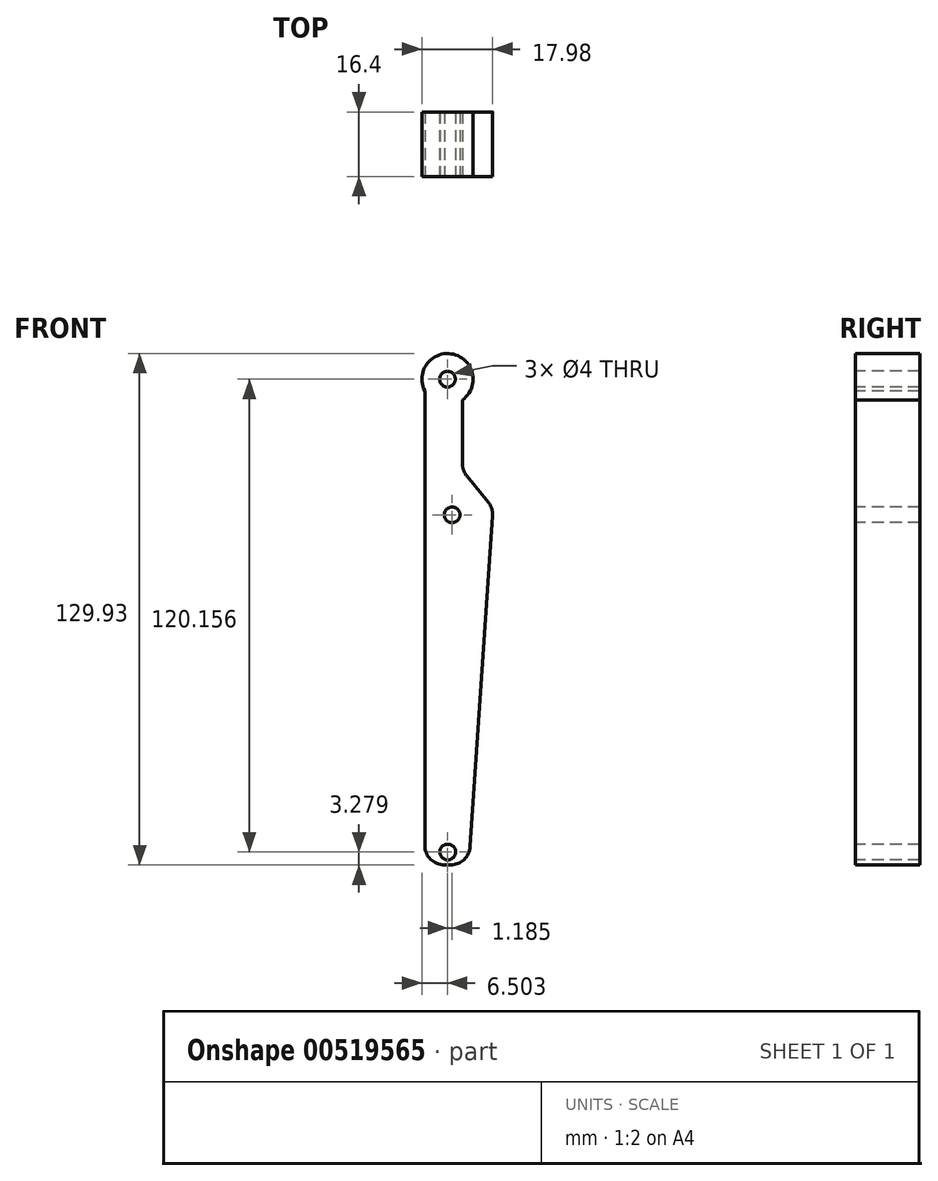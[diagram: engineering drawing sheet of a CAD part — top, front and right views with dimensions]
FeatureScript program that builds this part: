
annotation { "Feature Type Name" : "Feature", "Feature Type Description" : "" }
export const myFeature = defineFeature(function(context is Context, id is Id, definition is map)
    precondition{}
    {
        {
            var Q0;
            Q0=qCreatedBy(makeId("Front.planeOp"),FACE);
            var sketch = newSketch(context, id + "F0", { "sketchPlane" : qUnion([Q0])});
            skLineSegment(sketch, "E0", {"start": v(-46.45, 69) * mm, "end": v(-46.45, -52.6) * mm});
            skLineSegment(sketch, "E1", {"start": v(-41.45, -57.6) * mm, "end": v(-39.92, -57.6) * mm});
            skLineSegment(sketch, "E2", {"start": v(-34.93, -52.95) * mm, "end": v(-29.22, 31.01) * mm});
            skLineSegment(sketch, "E3", {"start": v(-30.33, 34.51) * mm, "end": v(-35.8, 41.22) * mm});
            skLineSegment(sketch, "E4", {"start": v(-36.91, 44.38) * mm, "end": v(-36.91, 62.6) * mm});
            skCircle(sketch, "E5", {"center": v(-40.69, 65.82) * mm, "radius": 6.5 * mm});
            skPoint(sketch, "E6.visualSharp", {"position": v(-46.45, -57.6) * mm});
            skArc(sketch, "E6.filletArc", {"start": v(-46.45, -52.6) * mm, "mid": v(-44.98, -56.14) * mm, "end": v(-41.45, -57.6) * mm});
            skPoint(sketch, "E7.visualSharp", {"position": v(-35.25, -57.6) * mm});
            skArc(sketch, "E7.filletArc", {"start": v(-39.92, -57.6) * mm, "mid": v(-36.5, -56.26) * mm, "end": v(-34.93, -52.95) * mm});
            skPoint(sketch, "E8.visualSharp", {"position": v(-29.08, 32.98) * mm});
            skArc(sketch, "E8.filletArc", {"start": v(-29.22, 31.01) * mm, "mid": v(-29.44, 32.87) * mm, "end": v(-30.33, 34.51) * mm});
            skPoint(sketch, "E9.visualSharp", {"position": v(-36.91, 42.6) * mm});
            skArc(sketch, "E9.filletArc", {"start": v(-36.91, 44.38) * mm, "mid": v(-36.63, 42.7) * mm, "end": v(-35.8, 41.22) * mm});
            skCircle(sketch, "E10", {"center": v(-40.62, -54.33) * mm, "radius": 2 * mm});
            skCircle(sketch, "E11", {"center": v(-40.69, 65.82) * mm, "radius": 2 * mm});
            skCircle(sketch, "E12", {"center": v(-39.5, 31.35) * mm, "radius": 2 * mm});
            skPoint(sketch, "E13.visualSharp", {"position": v(-33, 23.56) * mm});
            skPoint(sketch, "E14.visualSharp", {"position": v(-42.8, -43.29) * mm});
            skPoint(sketch, "E15.visualSharp", {"position": v(-37.55, -43.29) * mm});
            skPoint(sketch, "E16.visualSharp", {"position": v(-43.5, 57.41) * mm});
            skPoint(sketch, "E17.visualSharp", {"position": v(-39.5, 57.41) * mm});
            skPoint(sketch, "E18.visualSharp", {"position": v(-39.5, 37.41) * mm});
            skPoint(sketch, "E19.visualSharp", {"position": v(-43.5, 37.41) * mm});
            skSolve(sketch);
        }
        {
            var Q0;
            Q0 = qSketchRegion(id + "F0", true);
            extrude(context, id + "F1", {"entities" : qUnion([Q0]), "oppositeDirection" : true, "depth" : 8.4 * mm, "offsetDistance" : 25 * mm});
        }
        {
            var Q0;
            Q0 = qSketchRegion(id + "F0", true);
            extrude(context, id + "F2", {"entities" : qUnion([Q0]), "operationType" : NewBodyOperationType.ADD, "depth" : 8 * mm, "offsetDistance" : 25 * mm});
        }
    });
